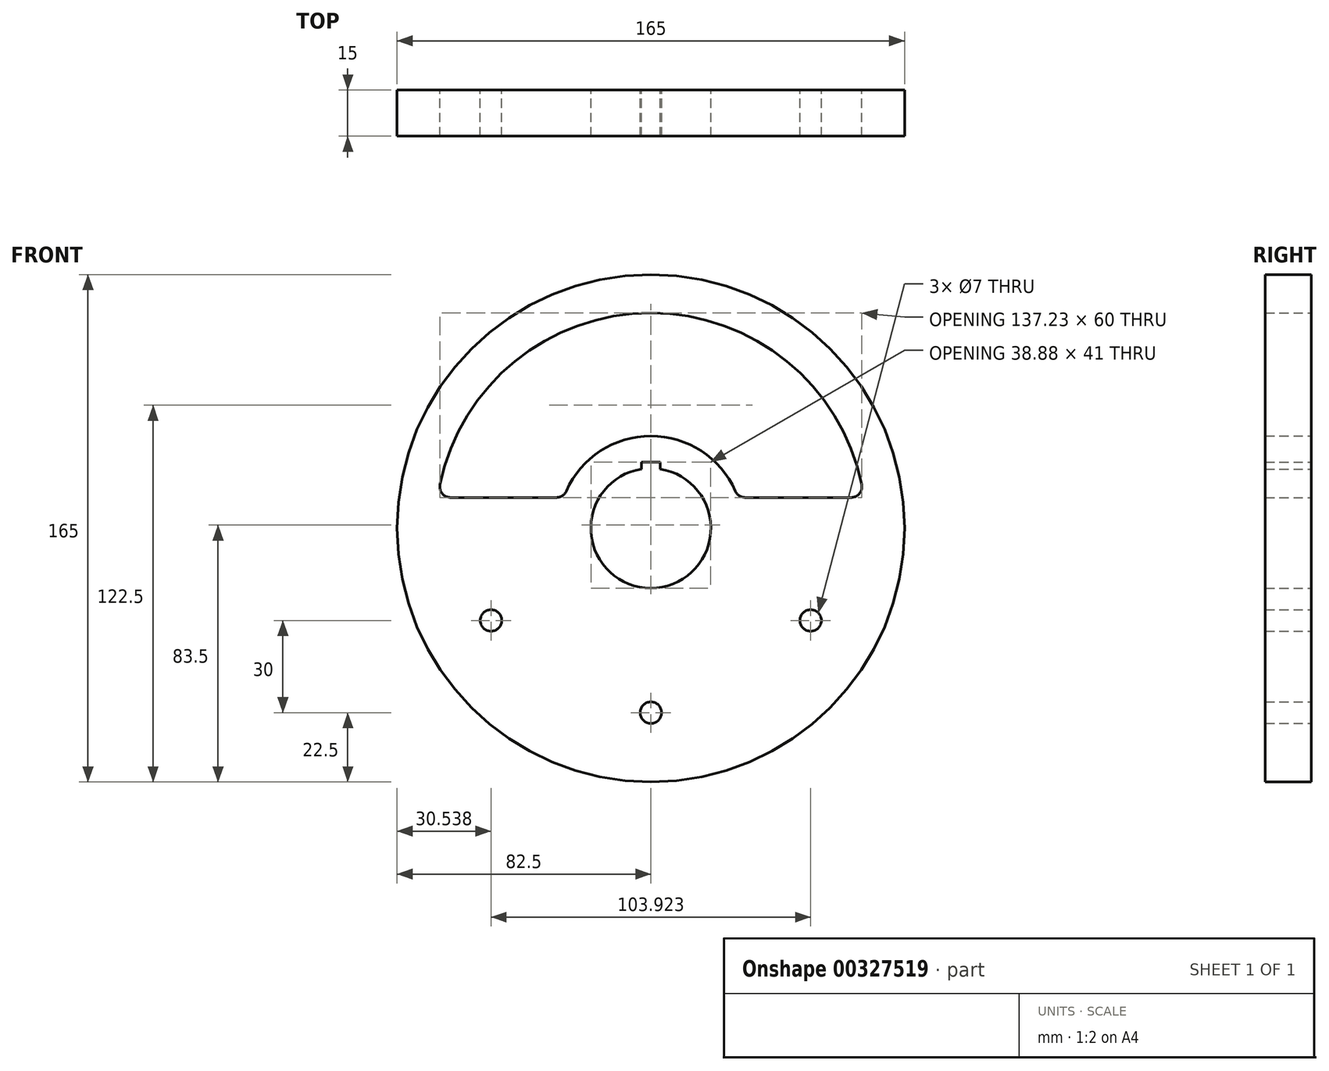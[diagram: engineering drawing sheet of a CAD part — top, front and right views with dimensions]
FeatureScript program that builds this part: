
annotation { "Feature Type Name" : "Feature", "Feature Type Description" : "" }
export const myFeature = defineFeature(function(context is Context, id is Id, definition is map)
    precondition{}
    {
        {
            var Q0;
            Q0=qCreatedBy(makeId("Front.planeOp"),FACE);
            var sketch = newSketch(context, id + "F0", { "sketchPlane" : qUnion([Q0])});
            skCircle(sketch, "E0", {"center": v(0, 0) * mm, "radius": 82.5 * mm});
            skLineSegment(sketch, "E1.trimOffspring", {"start": v(0, -55) * mm, "end": v(0, -60) * mm});
            skLineSegment(sketch, "E2", {"start": v(0, 0) * mm, "end": v(0, -12.5) * mm});
            skLineSegment(sketch, "E3", {"start": v(0, 0) * mm, "end": v(0, 19.5) * mm});
            skLineSegment(sketch, "E4", {"start": v(0, 19.5) * mm, "end": v(0, 21.5) * mm});
            skLineSegment(sketch, "E5", {"start": v(0, 21.5) * mm, "end": v(3, 21.5) * mm});
            skLineSegment(sketch, "E6", {"start": v(3, 21.5) * mm, "end": v(3, 19.27) * mm});
            skLineSegment(sketch, "E7.MirrorCS", {"start": v(0, 21.5) * mm, "end": v(-3, 21.5) * mm});
            skLineSegment(sketch, "E8.MirrorCS", {"start": v(-3, 21.5) * mm, "end": v(-3, 19.27) * mm});
            skLineSegment(sketch, "E9", {"start": v(0, 82.5) * mm, "end": v(0, -82.5) * mm, "construction": true});
            skLineSegment(sketch, "E10", {"start": v(82.5, 0) * mm, "end": v(-82.5, 0) * mm, "construction": true});
            skLineSegment(sketch, "E11", {"start": v(-69.28, 10) * mm, "end": v(-28.28, 10) * mm});
            skArc(sketch, "E12", {"start": v(-69.28, 10) * mm, "mid": v(0, -70) * mm, "end": v(69.28, 10) * mm, "construction": true});
            skArc(sketch, "E13", {"start": v(69.28, 10) * mm, "mid": v(0, 70) * mm, "end": v(-69.28, 10) * mm});
            skArc(sketch, "E14", {"start": v(-28.28, 10) * mm, "mid": v(0, -30) * mm, "end": v(28.28, 10) * mm, "construction": true});
            skArc(sketch, "E15", {"start": v(28.28, 10) * mm, "mid": v(0, 30) * mm, "end": v(-28.28, 10) * mm});
            skLineSegment(sketch, "E16.trimOffspring", {"start": v(28.28, 10) * mm, "end": v(69.28, 10) * mm});
            skLineSegment(sketch, "E17", {"start": v(0, 0) * mm, "end": v(51.96, -30) * mm});
            skCircle(sketch, "E18", {"center": v(51.96, -30) * mm, "radius": 3.5 * mm});
            skCircle(sketch, "E19.MirrorC", {"center": v(-51.96, -30) * mm, "radius": 3.5 * mm});
            skCircle(sketch, "E20", {"center": v(0, -60) * mm, "radius": 3.5 * mm});
            skCircle(sketch, "E21.converted", {"center": v(0, 0) * mm, "radius": 19.5 * mm});
            skPoint(sketch, "E22", {"position": v(3, 19.2) * mm});
            skSolve(sketch);
        }
        {
            var Q0;
            Q0=makeQuery(id+"F0.imprint","IMPRINT",FACE,{"disambiguationData":[TD([[makeQuery(id+"F0.imprint","IMPRINT",EDGE,{"derivedFrom":sQuery(id+"F0.wireOp",EDGE,"E0")}),1.0]])]});
            extrude(context, id + "F1", {"entities" : qUnion([Q0]), "depth" : 15 * mm});
        }
        {
            var Q0;
            Q0=makeQuery(id+"F1.opExtrude","SWEPT_EDGE",EDGE,{"disambiguationData":[OSD([sQuery(id+"F0.wireOp",EDGE,"E13"),sQuery(id+"F0.wireOp",EDGE,"E16.trimOffspring")])]});
            var Q1;
            Q1=makeQuery(id+"F1.opExtrude","SWEPT_EDGE",EDGE,{"disambiguationData":[OSD([sQuery(id+"F0.wireOp",EDGE,"E11"),sQuery(id+"F0.wireOp",EDGE,"E13")])]});
            var Q2;
            Q2=makeQuery(id+"F1.opExtrude","SWEPT_EDGE",EDGE,{"disambiguationData":[OSD([sQuery(id+"F0.wireOp",EDGE,"E11"),sQuery(id+"F0.wireOp",EDGE,"E15")])]});
            var Q3;
            Q3=makeQuery(id+"F1.opExtrude","SWEPT_EDGE",EDGE,{"disambiguationData":[OSD([sQuery(id+"F0.wireOp",EDGE,"E15"),sQuery(id+"F0.wireOp",EDGE,"E16.trimOffspring")])]});
            fillet(context, id + "F2", {"entities" : qUnion([Q0, Q1, Q2, Q3]), "radius" : 3.5 * mm, "tangentPropagation" : true, "allowEdgeOverflow" : false});
        }
    });
